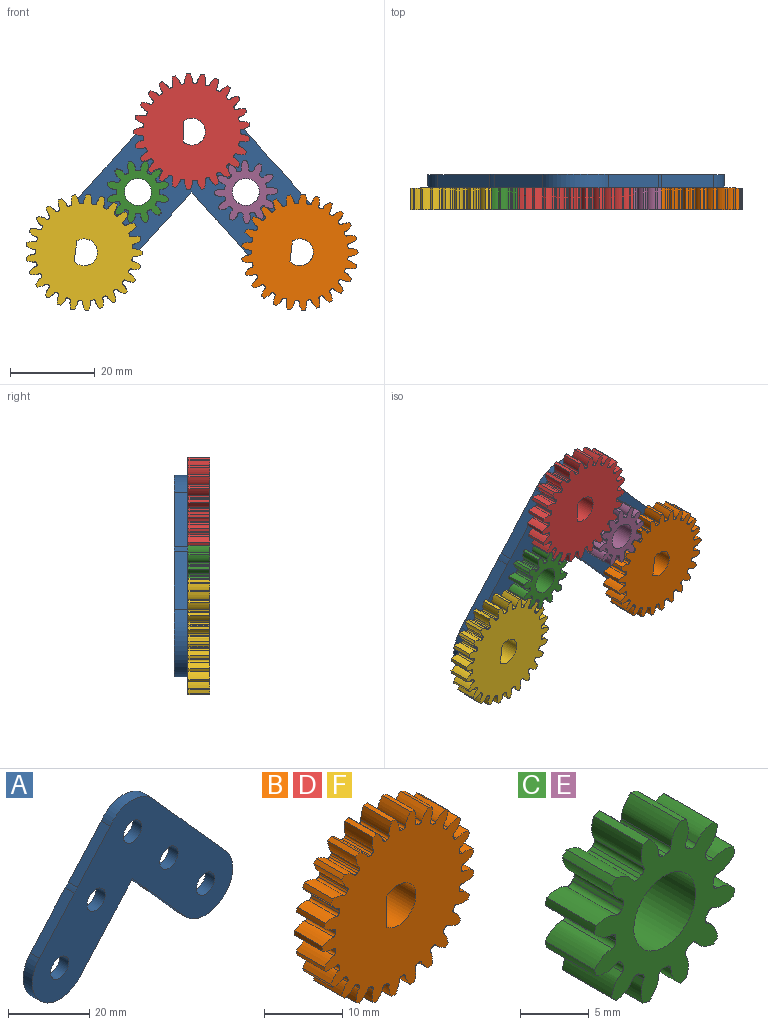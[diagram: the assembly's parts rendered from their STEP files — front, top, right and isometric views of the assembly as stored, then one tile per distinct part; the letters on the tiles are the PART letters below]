
ASSEMBLY  parts=6 mates=5
PART A: 22 faces, bbox 69.9x3.2x47.4 mm
  f0: cylinder r=9.53mm len=3.18mm, axis (0,1,0), area 9.5mm2, adj f1,f18,f20,f21
  f1: plane 5.16x4.62mm, normal (0.75,0,-0.67), area 22mm2, adj f0,f2,f20,f21
  f2: plane 6.21x5.56mm, normal (-0.75,0,-0.67), area 26.5mm2, adj f1,f3,f20,f21
  f3: cylinder r=9.53mm len=3.18mm, axis (0,1,0), area 1.2mm2, adj f2,f4,f20,f21
  f4: plane 13.86x12.4mm, normal (-0.75,0,-0.67), area 59.1mm2, adj f3,f5,f20,f21
  f5: cylinder r=9.53mm len=16.8mm, axis (0,1,0), area 95.9mm2, adj f4,f6,f20,f21
  f6: plane 13.76x12.33mm, normal (0.74,0,0.67), area 58.6mm2, adj f5,f7,f20,f21
  f7: cylinder r=9.53mm len=3.18mm, axis (0,1,0), area 3.7mm2, adj f6,f8,f20,f21
  f8: plane 13.15x11.78mm, normal (0.74,0,0.67), area 56mm2, adj f7,f9,f20,f21
  f9: cylinder r=9.53mm len=15.41mm, axis (0,1,0), area 57mm2, adj f8,f10,f20,f21
  f10: plane 12.73x11.42mm, normal (-0.74,0,0.67), area 54.3mm2, adj f9,f11,f20,f21
  f11: cylinder r=9.53mm len=3.18mm, axis (0,1,0), area 5.1mm2, adj f10,f12,f20,f21
  f12: plane 13.58x12.19mm, normal (-0.74,0,0.67), area 57.9mm2, adj f11,f13,f20,f21
  f13: cylinder r=9.53mm len=17.52mm, axis (0,1,0), area 99.8mm2, adj f12,f18,f20,f21
  f14: cylinder r=3.17mm len=6.35mm, axis (0,1,0), area 63.3mm2, adj f20,f21
  f15: cylinder r=3.17mm len=6.35mm, axis (0,1,0), area 63.3mm2, adj f20,f21
  f16: cylinder r=3.17mm len=6.35mm, axis (0,1,0), area 63.3mm2, adj f20,f21
  f17: cylinder r=3.17mm len=6.35mm, axis (0,1,0), area 63.3mm2, adj f20,f21
  f18: plane 11.99x10.72mm, normal (0.75,0,-0.67), area 51.1mm2, adj f0,f13,f20,f21
  f19: cylinder r=3.17mm len=6.35mm, axis (0,1,0), area 63.3mm2, adj f20,f21
  f20: plane 69.85x47.45mm, normal (0,-1,0), area 1548.4mm2, adj f0,f1,f2,f3,f4,f5,f6,f7
  f21: plane 69.85x47.45mm, normal (0,1,0), area 1548.4mm2, adj f0,f1,f2,f3,f4,f5,f6,f7
PART B: 154 faces, bbox 27.4x5.1x27.4 mm
  f0: cylinder r=13.72mm len=5.08mm, axis (0,1,0), area 3.7mm2, adj f24,f26,f137,f149
  f1: cylinder r=13.72mm len=5.08mm, axis (0,1,0), area 3.7mm2, adj f24,f26,f144,f147
  f2: cylinder r=13.72mm len=5.08mm, axis (0,1,0), area 3.7mm2, adj f24,f26,f132,f139
  f3: cylinder r=13.72mm len=5.08mm, axis (0,1,0), area 3.7mm2, adj f24,f26,f127,f134
  f4: cylinder r=13.72mm len=5.08mm, axis (0,1,0), area 3.7mm2, adj f24,f26,f122,f129
  f5: cylinder r=13.72mm len=5.08mm, axis (0,1,0), area 3.7mm2, adj f24,f26,f112,f124
  f6: cylinder r=13.72mm len=5.08mm, axis (0,1,0), area 3.7mm2, adj f24,f26,f107,f119
  f7: cylinder r=13.72mm len=5.08mm, axis (0,1,0), area 3.7mm2, adj f24,f26,f114,f117
  f8: cylinder r=13.72mm len=5.08mm, axis (0,1,0), area 3.7mm2, adj f24,f26,f102,f109
  f9: cylinder r=13.72mm len=5.08mm, axis (0,1,0), area 3.7mm2, adj f24,f26,f97,f104
  f10: cylinder r=13.72mm len=5.08mm, axis (0,1,0), area 3.7mm2, adj f24,f26,f92,f99
  f11: cylinder r=13.72mm len=5.08mm, axis (0,1,0), area 3.7mm2, adj f24,f26,f77,f94
  f12: cylinder r=13.72mm len=5.08mm, axis (0,1,0), area 3.7mm2, adj f24,f26,f27,f89
  f13: cylinder r=13.72mm len=5.08mm, axis (0,1,0), area 3.7mm2, adj f24,f26,f84,f87
  f14: cylinder r=13.72mm len=5.08mm, axis (0,1,0), area 3.7mm2, adj f24,f26,f72,f79
  f15: cylinder r=13.72mm len=5.08mm, axis (0,1,0), area 3.7mm2, adj f24,f26,f74,f82
  f16: cylinder r=13.72mm len=5.08mm, axis (0,1,0), area 3.7mm2, adj f24,f26,f69,f142
  f17: cylinder r=13.72mm len=5.08mm, axis (0,1,0), area 3.7mm2, adj f24,f26,f64,f67
  f18: cylinder r=13.72mm len=5.08mm, axis (0,1,0), area 3.7mm2, adj f24,f26,f59,f62
  f19: cylinder r=13.72mm len=5.08mm, axis (0,1,0), area 3.7mm2, adj f24,f26,f54,f57
  f20: cylinder r=13.72mm len=5.08mm, axis (0,1,0), area 3.7mm2, adj f24,f26,f42,f49
  f21: cylinder r=13.72mm len=5.08mm, axis (0,1,0), area 3.7mm2, adj f24,f26,f32,f44
  f22: cylinder r=13.72mm len=5.08mm, axis (0,1,0), area 3.7mm2, adj f24,f26,f39,f52
  f23: cylinder r=13.72mm len=5.08mm, axis (0,1,0), area 3.7mm2, adj f24,f26,f34,f37
  f24: plane 27.42x27.37mm, normal (0,-1,0), area 471.4mm2, adj f0,f1,f2,f3,f4,f5,f6,f7
  f25: cylinder r=13.72mm len=5.08mm, axis (0,1,0), area 3.7mm2, adj f24,f26,f29,f47
  f26: plane 27.42x27.37mm, normal (0,1,0), area 471.4mm2, adj f0,f1,f2,f3,f4,f5,f6,f7
  f27: extruded ~5.08x1.85mm, area 10.4mm2, adj f12,f24,f26,f30
  f28: cylinder r=11.43mm len=5.08mm, axis (0,1,0), area 1.8mm2, adj f24,f26,f30,f31
  f29: extruded ~5.08x1.85mm, area 10.4mm2, adj f24,f25,f26,f31
  f30: cylinder r=0.38mm len=5.08mm, axis (0,1,0), area 3mm2, adj f24,f26,f27,f28
  f31: cylinder r=0.38mm len=5.08mm, axis (0,1,0), area 3mm2, adj f24,f26,f28,f29
  f32: extruded ~5.08x1.89mm, area 10.4mm2, adj f21,f24,f26,f35
  f33: cylinder r=11.43mm len=5.08mm, axis (0,1,0), area 1.8mm2, adj f24,f26,f35,f36
  f34: extruded ~5.08x1.85mm, area 10.4mm2, adj f23,f24,f26,f36
  f35: cylinder r=0.38mm len=5.08mm, axis (0,1,0), area 3mm2, adj f24,f26,f32,f33
  f36: cylinder r=0.38mm len=5.08mm, axis (0,1,0), area 3mm2, adj f24,f26,f33,f34
  f37: extruded ~5.08x1.66mm, area 10.4mm2, adj f23,f24,f26,f40
  f38: cylinder r=11.43mm len=5.08mm, axis (0,1,0), area 1.8mm2, adj f24,f26,f40,f41
  f39: extruded ~5.08x1.99mm, area 10.4mm2, adj f22,f24,f26,f41
  f40: cylinder r=0.38mm len=5.08mm, axis (0,1,0), area 3mm2, adj f24,f26,f37,f38
  f41: cylinder r=0.38mm len=5.08mm, axis (0,1,0), area 3mm2, adj f24,f26,f38,f39
  f42: extruded ~5.08x2.01mm, area 10.4mm2, adj f20,f24,f26,f45
  f43: cylinder r=11.43mm len=5.08mm, axis (0,1,0), area 1.8mm2, adj f24,f26,f45,f46
  f44: extruded ~5.08x1.59mm, area 10.4mm2, adj f21,f24,f26,f46
  f45: cylinder r=0.38mm len=5.08mm, axis (0,1,0), area 3mm2, adj f24,f26,f42,f43
  f46: cylinder r=0.38mm len=5.08mm, axis (0,1,0), area 3mm2, adj f24,f26,f43,f44
  f47: extruded ~5.08x1.99mm, area 10.4mm2, adj f24,f25,f26,f50
  f48: cylinder r=11.43mm len=5.08mm, axis (0,1,0), area 1.8mm2, adj f24,f26,f50,f51
  f49: extruded ~5.08x1.6mm, area 10.4mm2, adj f20,f24,f26,f51
  f50: cylinder r=0.38mm len=5.08mm, axis (0,1,0), area 3mm2, adj f24,f26,f47,f48
  f51: cylinder r=0.38mm len=5.08mm, axis (0,1,0), area 3mm2, adj f24,f26,f48,f49
  f52: extruded ~5.08x1.52mm, area 10.4mm2, adj f22,f24,f26,f55
  f53: cylinder r=11.43mm len=5.08mm, axis (0,1,0), area 1.8mm2, adj f24,f26,f55,f56
  f54: extruded ~5.08x2.01mm, area 10.4mm2, adj f19,f24,f26,f56
  f55: cylinder r=0.38mm len=5.08mm, axis (0,1,0), area 3mm2, adj f24,f26,f52,f53
  f56: cylinder r=0.38mm len=5.08mm, axis (0,1,0), area 3mm2, adj f24,f26,f53,f54
  f57: extruded ~5.08x1.8mm, area 10.4mm2, adj f19,f24,f26,f60
  f58: cylinder r=11.43mm len=5.08mm, axis (0,1,0), area 1.8mm2, adj f24,f26,f60,f61
  f59: extruded ~5.08x1.9mm, area 10.4mm2, adj f18,f24,f26,f61
  f60: cylinder r=0.38mm len=5.08mm, axis (0,1,0), area 3mm2, adj f24,f26,f57,f58
  f61: cylinder r=0.38mm len=5.08mm, axis (0,1,0), area 3mm2, adj f24,f26,f58,f59
  f62: extruded ~5.08x1.97mm, area 10.4mm2, adj f18,f24,f26,f65
  f63: cylinder r=11.43mm len=5.08mm, axis (0,1,0), area 1.8mm2, adj f24,f26,f65,f66
  f64: extruded ~5.08x1.67mm, area 10.4mm2, adj f17,f24,f26,f66
  f65: cylinder r=0.38mm len=5.08mm, axis (0,1,0), area 3mm2, adj f24,f26,f62,f63
  f66: cylinder r=0.38mm len=5.08mm, axis (0,1,0), area 3mm2, adj f24,f26,f63,f64
  f67: extruded ~5.08x2.02mm, area 10.4mm2, adj f17,f24,f26,f70
  f68: cylinder r=11.43mm len=5.08mm, axis (0,1,0), area 1.8mm2, adj f24,f26,f70,f71
  f69: extruded ~5.08x1.51mm, area 10.4mm2, adj f16,f24,f26,f71
  f70: cylinder r=0.38mm len=5.08mm, axis (0,1,0), area 3mm2, adj f24,f26,f67,f68
  f71: cylinder r=0.38mm len=5.08mm, axis (0,1,0), area 3mm2, adj f24,f26,f68,f69
  f72: extruded ~5.08x1.85mm, area 10.4mm2, adj f14,f24,f26,f75
  f73: cylinder r=11.43mm len=5.08mm, axis (0,1,0), area 1.8mm2, adj f24,f26,f75,f76
  f74: extruded ~5.08x1.89mm, area 10.4mm2, adj f15,f24,f26,f76
  f75: cylinder r=0.38mm len=5.08mm, axis (0,1,0), area 3mm2, adj f24,f26,f72,f73
  f76: cylinder r=0.38mm len=5.08mm, axis (0,1,0), area 3mm2, adj f24,f26,f73,f74
  f77: extruded ~5.08x1.99mm, area 10.4mm2, adj f11,f24,f26,f80
  f78: cylinder r=11.43mm len=5.08mm, axis (0,1,0), area 1.8mm2, adj f24,f26,f80,f81
  f79: extruded ~5.08x1.66mm, area 10.4mm2, adj f14,f24,f26,f81
  f80: cylinder r=0.38mm len=5.08mm, axis (0,1,0), area 3mm2, adj f24,f26,f77,f78
  f81: cylinder r=0.38mm len=5.08mm, axis (0,1,0), area 3mm2, adj f24,f26,f78,f79
  f82: extruded ~5.08x1.59mm, area 10.4mm2, adj f15,f24,f26,f85
  f83: cylinder r=11.43mm len=5.08mm, axis (0,1,0), area 1.8mm2, adj f24,f26,f85,f86
  f84: extruded ~5.08x2.01mm, area 10.4mm2, adj f13,f24,f26,f86
  f85: cylinder r=0.38mm len=5.08mm, axis (0,1,0), area 3mm2, adj f24,f26,f82,f83
  f86: cylinder r=0.38mm len=5.08mm, axis (0,1,0), area 3mm2, adj f24,f26,f83,f84
  f87: extruded ~5.08x1.6mm, area 10.4mm2, adj f13,f24,f26,f90
  f88: cylinder r=11.43mm len=5.08mm, axis (0,1,0), area 1.8mm2, adj f24,f26,f90,f91
  f89: extruded ~5.08x1.99mm, area 10.4mm2, adj f12,f24,f26,f91
  f90: cylinder r=0.38mm len=5.08mm, axis (0,1,0), area 3mm2, adj f24,f26,f87,f88
  f91: cylinder r=0.38mm len=5.08mm, axis (0,1,0), area 3mm2, adj f24,f26,f88,f89
  f92: extruded ~5.08x2.01mm, area 10.4mm2, adj f10,f24,f26,f95
  f93: cylinder r=11.43mm len=5.08mm, axis (0,1,0), area 1.8mm2, adj f24,f26,f95,f96
  f94: extruded ~5.08x1.52mm, area 10.4mm2, adj f11,f24,f26,f96
  f95: cylinder r=0.38mm len=5.08mm, axis (0,1,0), area 3mm2, adj f24,f26,f92,f93
  f96: cylinder r=0.38mm len=5.08mm, axis (0,1,0), area 3mm2, adj f24,f26,f93,f94
  f97: extruded ~5.08x1.9mm, area 10.4mm2, adj f9,f24,f26,f100
  f98: cylinder r=11.43mm len=5.08mm, axis (0,1,0), area 1.8mm2, adj f24,f26,f100,f101
  f99: extruded ~5.08x1.8mm, area 10.4mm2, adj f10,f24,f26,f101
  f100: cylinder r=0.38mm len=5.08mm, axis (0,1,0), area 3mm2, adj f24,f26,f97,f98
  f101: cylinder r=0.38mm len=5.08mm, axis (0,1,0), area 3mm2, adj f24,f26,f98,f99
  f102: extruded ~5.08x1.67mm, area 10.4mm2, adj f8,f24,f26,f105
  f103: cylinder r=11.43mm len=5.08mm, axis (0,1,0), area 1.8mm2, adj f24,f26,f105,f106
  f104: extruded ~5.08x1.97mm, area 10.4mm2, adj f9,f24,f26,f106
  f105: cylinder r=0.38mm len=5.08mm, axis (0,1,0), area 3mm2, adj f24,f26,f102,f103
  f106: cylinder r=0.38mm len=5.08mm, axis (0,1,0), area 3mm2, adj f24,f26,f103,f104
  f107: extruded ~5.08x1.51mm, area 10.4mm2, adj f6,f24,f26,f110
  f108: cylinder r=11.43mm len=5.08mm, axis (0,1,0), area 1.8mm2, adj f24,f26,f110,f111
  f109: extruded ~5.08x2.02mm, area 10.4mm2, adj f8,f24,f26,f111
  f110: cylinder r=0.38mm len=5.08mm, axis (0,1,0), area 3mm2, adj f24,f26,f107,f108
  f111: cylinder r=0.38mm len=5.08mm, axis (0,1,0), area 3mm2, adj f24,f26,f108,f109
  f112: extruded ~5.08x1.97mm, area 10.4mm2, adj f5,f24,f26,f115
  f113: cylinder r=11.43mm len=5.08mm, axis (0,1,0), area 1.8mm2, adj f24,f26,f115,f116
  f114: extruded ~5.08x1.73mm, area 10.4mm2, adj f7,f24,f26,f116
  f115: cylinder r=0.38mm len=5.08mm, axis (0,1,0), area 3mm2, adj f24,f26,f112,f113
  f116: cylinder r=0.38mm len=5.08mm, axis (0,1,0), area 3mm2, adj f24,f26,f113,f114
  f117: extruded ~5.08x1.79mm, area 10.4mm2, adj f7,f24,f26,f120
  f118: cylinder r=11.43mm len=5.08mm, axis (0,1,0), area 1.8mm2, adj f24,f26,f120,f121
  f119: extruded ~5.08x1.93mm, area 10.4mm2, adj f6,f24,f26,f121
  f120: cylinder r=0.38mm len=5.08mm, axis (0,1,0), area 3mm2, adj f24,f26,f117,f118
  f121: cylinder r=0.38mm len=5.08mm, axis (0,1,0), area 3mm2, adj f24,f26,f118,f119
  f122: extruded ~5.08x2.02mm, area 10.4mm2, adj f4,f24,f26,f125
  f123: cylinder r=11.43mm len=5.08mm, axis (0,1,0), area 1.8mm2, adj f24,f26,f125,f126
  f124: extruded ~5.08x1.43mm, area 10.4mm2, adj f5,f24,f26,f126
  f125: cylinder r=0.38mm len=5.08mm, axis (0,1,0), area 3mm2, adj f24,f26,f122,f123
  f126: cylinder r=0.38mm len=5.08mm, axis (0,1,0), area 3mm2, adj f24,f26,f123,f124
  f127: extruded ~5.08x1.94mm, area 10.4mm2, adj f3,f24,f26,f130
  f128: cylinder r=11.43mm len=5.08mm, axis (0,1,0), area 1.8mm2, adj f24,f26,f130,f131
  f129: extruded ~5.08x1.74mm, area 10.4mm2, adj f4,f24,f26,f131
  f130: cylinder r=0.38mm len=5.08mm, axis (0,1,0), area 3mm2, adj f24,f26,f127,f128
  f131: cylinder r=0.38mm len=5.08mm, axis (0,1,0), area 3mm2, adj f24,f26,f128,f129
  f132: extruded ~5.08x1.74mm, area 10.4mm2, adj f2,f24,f26,f135
  f133: cylinder r=11.43mm len=5.08mm, axis (0,1,0), area 1.8mm2, adj f24,f26,f135,f136
  f134: extruded ~5.08x1.94mm, area 10.4mm2, adj f3,f24,f26,f136
  f135: cylinder r=0.38mm len=5.08mm, axis (0,1,0), area 3mm2, adj f24,f26,f132,f133
  f136: cylinder r=0.38mm len=5.08mm, axis (0,1,0), area 3mm2, adj f24,f26,f133,f134
  f137: extruded ~5.08x1.43mm, area 10.4mm2, adj f0,f24,f26,f140
  f138: cylinder r=11.43mm len=5.08mm, axis (0,1,0), area 1.8mm2, adj f24,f26,f140,f141
  f139: extruded ~5.08x2.02mm, area 10.4mm2, adj f2,f24,f26,f141
  f140: cylinder r=0.38mm len=5.08mm, axis (0,1,0), area 3mm2, adj f24,f26,f137,f138
  f141: cylinder r=0.38mm len=5.08mm, axis (0,1,0), area 3mm2, adj f24,f26,f138,f139
  f142: extruded ~5.08x1.93mm, area 10.4mm2, adj f16,f24,f26,f145
  f143: cylinder r=11.43mm len=5.08mm, axis (0,1,0), area 1.8mm2, adj f24,f26,f145,f146
  f144: extruded ~5.08x1.79mm, area 10.4mm2, adj f1,f24,f26,f146
  f145: cylinder r=0.38mm len=5.08mm, axis (0,1,0), area 3mm2, adj f24,f26,f142,f143
  f146: cylinder r=0.38mm len=5.08mm, axis (0,1,0), area 3mm2, adj f24,f26,f143,f144
  f147: extruded ~5.08x1.73mm, area 10.4mm2, adj f1,f24,f26,f150
  f148: cylinder r=11.43mm len=5.08mm, axis (0,1,0), area 1.8mm2, adj f24,f26,f150,f151
  f149: extruded ~5.08x1.97mm, area 10.4mm2, adj f0,f24,f26,f151
  f150: cylinder r=0.38mm len=5.08mm, axis (0,1,0), area 3mm2, adj f24,f26,f147,f148
  f151: cylinder r=0.38mm len=5.08mm, axis (0,1,0), area 3mm2, adj f24,f26,f148,f149
  f152: plane 5.08x4.88mm, normal (1,0,0), area 24.8mm2, adj f24,f26,f153
  f153: cylinder r=3.17mm len=6.35mm, axis (0,-1,0), area 73.1mm2, adj f24,f26,f152
PART C: 75 faces, bbox 14.5x5.1x14.5 mm
  f0: cylinder r=7.41mm len=5.08mm, axis (0,1,0), area 3.3mm2, adj f11,f13,f59,f71
  f1: cylinder r=7.41mm len=5.08mm, axis (0,1,0), area 3.3mm2, adj f11,f13,f66,f69
  f2: cylinder r=7.41mm len=5.08mm, axis (0,1,0), area 3.3mm2, adj f11,f13,f54,f61
  f3: cylinder r=7.41mm len=5.08mm, axis (0,1,0), area 3.3mm2, adj f11,f13,f49,f56
  f4: cylinder r=7.41mm len=5.08mm, axis (0,1,0), area 3.3mm2, adj f11,f13,f44,f51
  f5: cylinder r=7.41mm len=5.08mm, axis (0,1,0), area 3.3mm2, adj f11,f13,f34,f46
  f6: cylinder r=7.41mm len=5.08mm, axis (0,1,0), area 3.3mm2, adj f11,f13,f14,f41
  f7: cylinder r=7.41mm len=5.08mm, axis (0,1,0), area 3.3mm2, adj f11,f13,f36,f39
  f8: cylinder r=7.41mm len=5.08mm, axis (0,1,0), area 3.3mm2, adj f11,f13,f24,f31
  f9: cylinder r=7.41mm len=5.08mm, axis (0,1,0), area 3.3mm2, adj f11,f13,f19,f26
  f10: cylinder r=7.41mm len=5.08mm, axis (0,1,0), area 3.3mm2, adj f11,f13,f21,f64
  f11: plane 14.5x14.5mm, normal (0,-1,0), area 90.3mm2, adj f0,f1,f2,f3,f4,f5,f6,f7
  f12: cylinder r=7.41mm len=5.08mm, axis (0,1,0), area 3.3mm2, adj f11,f13,f16,f29
  f13: plane 14.5x14.5mm, normal (0,1,0), area 90.3mm2, adj f0,f1,f2,f3,f4,f5,f6,f7
  f14: extruded ~5.08x1.82mm, area 10.8mm2, adj f6,f11,f13,f17
  f15: cylinder r=5.03mm len=5.08mm, axis (0,1,0), area 1.8mm2, adj f11,f13,f17,f18
  f16: extruded ~5.08x1.82mm, area 10.8mm2, adj f11,f12,f13,f18
  f17: cylinder r=0.44mm len=5.08mm, axis (0,1,0), area 3.3mm2, adj f11,f13,f14,f15
  f18: cylinder r=0.44mm len=5.08mm, axis (0,1,0), area 3.3mm2, adj f11,f13,f15,f16
  f19: extruded ~5.08x1.82mm, area 10.8mm2, adj f9,f11,f13,f22
  f20: cylinder r=5.03mm len=5.08mm, axis (0,1,0), area 1.8mm2, adj f11,f13,f22,f23
  f21: extruded ~5.08x1.82mm, area 10.8mm2, adj f10,f11,f13,f23
  f22: cylinder r=0.44mm len=5.08mm, axis (0,1,0), area 3.3mm2, adj f11,f13,f19,f20
  f23: cylinder r=0.44mm len=5.08mm, axis (0,1,0), area 3.3mm2, adj f11,f13,f20,f21
  f24: extruded ~5.08x1.75mm, area 10.8mm2, adj f8,f11,f13,f27
  f25: cylinder r=5.03mm len=5.08mm, axis (0,1,0), area 1.8mm2, adj f11,f13,f27,f28
  f26: extruded ~5.08x2.06mm, area 10.8mm2, adj f9,f11,f13,f28
  f27: cylinder r=0.44mm len=5.08mm, axis (0,1,0), area 3.3mm2, adj f11,f13,f24,f25
  f28: cylinder r=0.44mm len=5.08mm, axis (0,1,0), area 3.3mm2, adj f11,f13,f25,f26
  f29: extruded ~5.08x2.06mm, area 10.8mm2, adj f11,f12,f13,f32
  f30: cylinder r=5.03mm len=5.08mm, axis (0,1,0), area 1.8mm2, adj f11,f13,f32,f33
  f31: extruded ~5.08x1.75mm, area 10.8mm2, adj f8,f11,f13,f33
  f32: cylinder r=0.44mm len=5.08mm, axis (0,1,0), area 3.3mm2, adj f11,f13,f29,f30
  f33: cylinder r=0.44mm len=5.08mm, axis (0,1,0), area 3.3mm2, adj f11,f13,f30,f31
  f34: extruded ~5.08x2.06mm, area 10.8mm2, adj f5,f11,f13,f37
  f35: cylinder r=5.03mm len=5.08mm, axis (0,1,0), area 1.8mm2, adj f11,f13,f37,f38
  f36: extruded ~5.08x1.75mm, area 10.8mm2, adj f7,f11,f13,f38
  f37: cylinder r=0.44mm len=5.08mm, axis (0,1,0), area 3.3mm2, adj f11,f13,f34,f35
  f38: cylinder r=0.44mm len=5.08mm, axis (0,1,0), area 3.3mm2, adj f11,f13,f35,f36
  f39: extruded ~5.08x1.75mm, area 10.8mm2, adj f7,f11,f13,f42
  f40: cylinder r=5.03mm len=5.08mm, axis (0,1,0), area 1.8mm2, adj f11,f13,f42,f43
  f41: extruded ~5.08x2.06mm, area 10.8mm2, adj f6,f11,f13,f43
  f42: cylinder r=0.44mm len=5.08mm, axis (0,1,0), area 3.3mm2, adj f11,f13,f39,f40
  f43: cylinder r=0.44mm len=5.08mm, axis (0,1,0), area 3.3mm2, adj f11,f13,f40,f41
  f44: extruded ~5.08x1.82mm, area 10.8mm2, adj f4,f11,f13,f47
  f45: cylinder r=5.03mm len=5.08mm, axis (0,1,0), area 1.8mm2, adj f11,f13,f47,f48
  f46: extruded ~5.08x1.82mm, area 10.8mm2, adj f5,f11,f13,f48
  f47: cylinder r=0.44mm len=5.08mm, axis (0,1,0), area 3.3mm2, adj f11,f13,f44,f45
  f48: cylinder r=0.44mm len=5.08mm, axis (0,1,0), area 3.3mm2, adj f11,f13,f45,f46
  f49: extruded ~5.08x1.75mm, area 10.8mm2, adj f3,f11,f13,f52
  f50: cylinder r=5.03mm len=5.08mm, axis (0,1,0), area 1.8mm2, adj f11,f13,f52,f53
  f51: extruded ~5.08x2.06mm, area 10.8mm2, adj f4,f11,f13,f53
  f52: cylinder r=0.44mm len=5.08mm, axis (0,1,0), area 3.3mm2, adj f11,f13,f49,f50
  f53: cylinder r=0.44mm len=5.08mm, axis (0,1,0), area 3.3mm2, adj f11,f13,f50,f51
  f54: extruded ~5.08x2.06mm, area 10.8mm2, adj f2,f11,f13,f57
  f55: cylinder r=5.03mm len=5.08mm, axis (0,1,0), area 1.8mm2, adj f11,f13,f57,f58
  f56: extruded ~5.08x1.75mm, area 10.8mm2, adj f3,f11,f13,f58
  f57: cylinder r=0.44mm len=5.08mm, axis (0,1,0), area 3.3mm2, adj f11,f13,f54,f55
  f58: cylinder r=0.44mm len=5.08mm, axis (0,1,0), area 3.3mm2, adj f11,f13,f55,f56
  f59: extruded ~5.08x1.82mm, area 10.8mm2, adj f0,f11,f13,f62
  f60: cylinder r=5.03mm len=5.08mm, axis (0,1,0), area 1.8mm2, adj f11,f13,f62,f63
  f61: extruded ~5.08x1.82mm, area 10.8mm2, adj f2,f11,f13,f63
  f62: cylinder r=0.44mm len=5.08mm, axis (0,1,0), area 3.3mm2, adj f11,f13,f59,f60
  f63: cylinder r=0.44mm len=5.08mm, axis (0,1,0), area 3.3mm2, adj f11,f13,f60,f61
  f64: extruded ~5.08x2.06mm, area 10.8mm2, adj f10,f11,f13,f67
  f65: cylinder r=5.03mm len=5.08mm, axis (0,1,0), area 1.8mm2, adj f11,f13,f67,f68
  f66: extruded ~5.08x1.75mm, area 10.8mm2, adj f1,f11,f13,f68
  f67: cylinder r=0.44mm len=5.08mm, axis (0,1,0), area 3.3mm2, adj f11,f13,f64,f65
  f68: cylinder r=0.44mm len=5.08mm, axis (0,1,0), area 3.3mm2, adj f11,f13,f65,f66
  f69: extruded ~5.08x1.75mm, area 10.8mm2, adj f1,f11,f13,f72
  f70: cylinder r=5.03mm len=5.08mm, axis (0,1,0), area 1.8mm2, adj f11,f13,f72,f73
  f71: extruded ~5.08x2.06mm, area 10.8mm2, adj f0,f11,f13,f73
  f72: cylinder r=0.44mm len=5.08mm, axis (0,1,0), area 3.3mm2, adj f11,f13,f69,f70
  f73: cylinder r=0.44mm len=5.08mm, axis (0,1,0), area 3.3mm2, adj f11,f13,f70,f71
  f74: cylinder r=3.17mm len=6.35mm, axis (0,-1,0), area 101.3mm2, adj f11,f13
PART D: same geometry as B
PART E: same geometry as C
PART F: same geometry as B
PLACE A t=(0.53,17.79,6.08)mm fixed
PLACE B rot(axis=(0,1,0),7.1deg) t=(25.93,14.61,9.64)mm
PLACE C t=(-12.17,14.61,23.84)mm
PLACE D t=(0.53,14.61,38.04)mm
PLACE E rot(axis=(0,1,0),13.2deg) t=(13.23,14.61,23.84)mm
PLACE F rot(axis=(0,1,0),7.8deg) t=(-24.87,14.61,9.64)mm
MATE revolute D.f0 <-> A.f17  axis (0,1,0) through (0.53,14.61,38.04)mm
MATE revolute F.f0 <-> A.f13  axis (0,1,0) through (-24.87,14.61,9.64)mm
MATE revolute A.f3 <-> E.f74  axis (0,-1,0) through (13.23,14.61,23.84)mm
MATE revolute C.f74 <-> A.f0  axis (0,-1,0) through (-12.17,14.61,23.84)mm
MATE revolute B.f0 <-> A.f5  axis (0,1,0) through (25.93,14.61,9.64)mm
